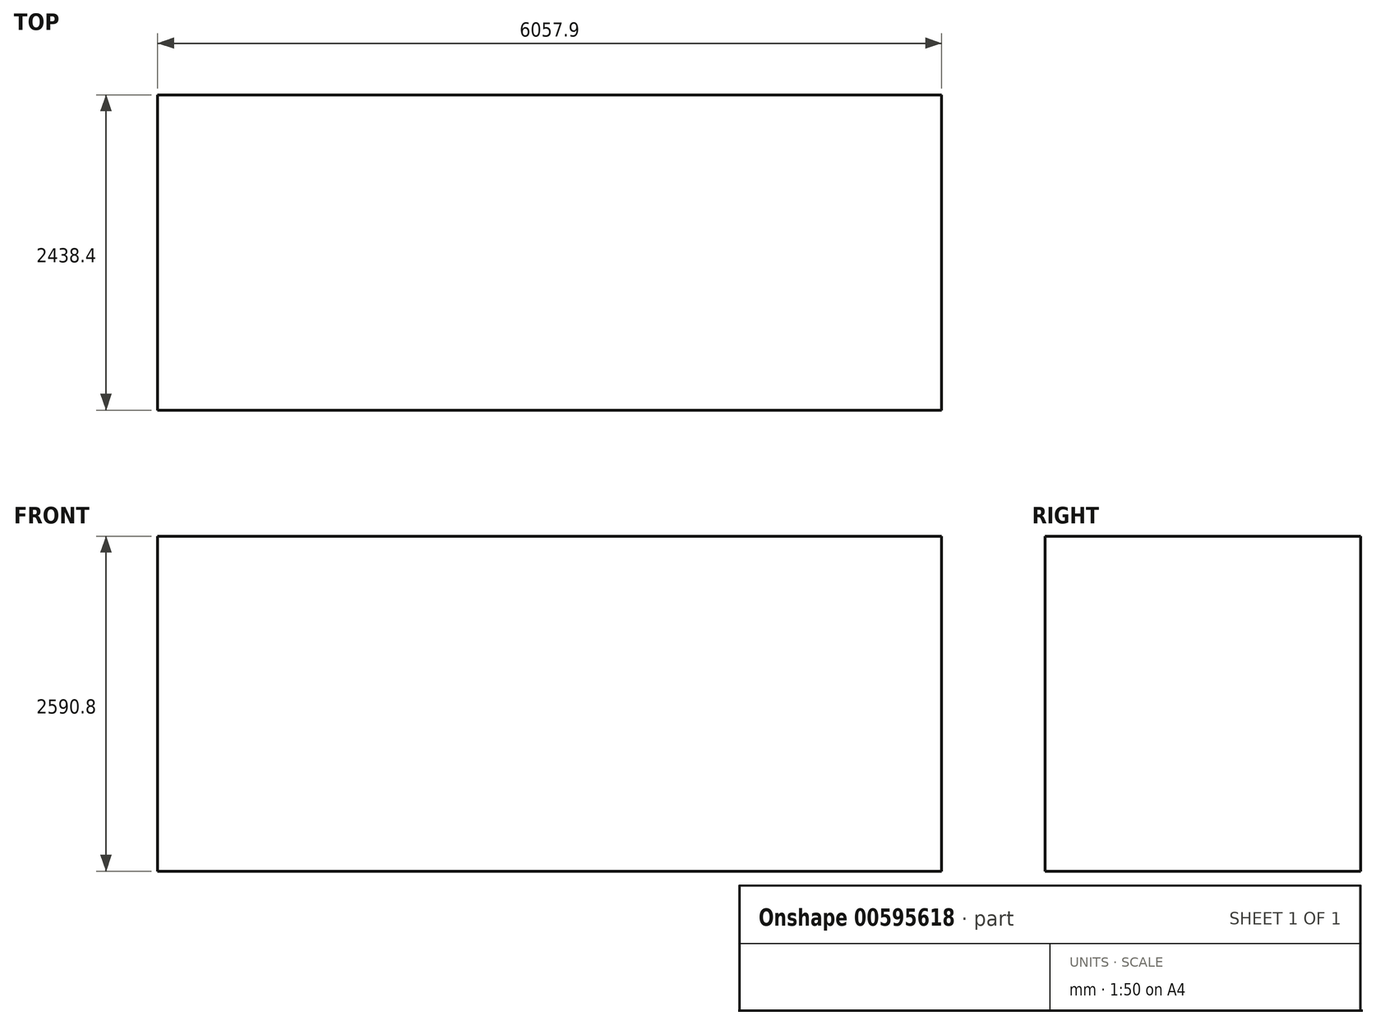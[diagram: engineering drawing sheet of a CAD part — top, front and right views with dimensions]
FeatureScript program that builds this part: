
annotation { "Feature Type Name" : "Feature", "Feature Type Description" : "" }
export const myFeature = defineFeature(function(context is Context, id is Id, definition is map)
    precondition{}
    {
        {
            var Q0;
            Q0=qCreatedBy(makeId("Top.planeOp"),FACE);
            var sketch = newSketch(context, id + "F0", { "sketchPlane" : qUnion([Q0])});
            skLineSegment(sketch, "E0.bottom", {"start": v(0, 0) * mm, "end": v(12192, 0) * mm});
            skLineSegment(sketch, "E0.top", {"start": v(0, 2438.4) * mm, "end": v(12192, 2438.4) * mm});
            skLineSegment(sketch, "E0.left", {"start": v(0, 0) * mm, "end": v(0, 2438.4) * mm});
            skLineSegment(sketch, "E0.right", {"start": v(12192, 0) * mm, "end": v(12192, 2438.4) * mm});
            skSolve(sketch);
        }
        {
            var Q0;
            Q0=makeQuery(id+"F0.imprint","IMPRINT",FACE,{"disambiguationData":[TD([[makeQuery(id+"F0.imprint","IMPRINT",EDGE,{"derivedFrom":sQuery(id+"F0.wireOp",EDGE,"E0.bottom")}),1.0]])]});
            extrude(context, id + "F1", {"entities" : qUnion([Q0]), "depth" : 2590.8 * mm, "offsetDistance" : 30.48 * mm});
        }
        {
            var Q0;
            Q0=makeQuery(id+"F1.opExtrude","SWEPT_BODY",BODY,{"disambiguationData":[OSD([sQuery(id+"F0.wireOp",EDGE,"E0.bottom"),sQuery(id+"F0.wireOp",EDGE,"E0.top"),sQuery(id+"F0.wireOp",EDGE,"E0.left"),sQuery(id+"F0.wireOp",EDGE,"E0.right")])]});
            transform(context, id + "F2", {"entities" : qUnion([Q0]), "transformType" : TransformType.COPY});
        }
        {
            var Q0;
            Q0=makeQuery(id+"F2.opPattern","COPY",FACE,{"derivedFrom":makeQuery(id+"F1.opExtrude","SWEPT_FACE",FACE,{"disambiguationData":[OSD([sQuery(id+"F0.wireOp",EDGE,"E0.right")])]}),"instanceName":"1"});
            extrude(context, id + "F3", {"entities" : qUnion([Q0]), "operationType" : NewBodyOperationType.REMOVE, "oppositeDirection" : true, "depth" : 6096 * mm + 38.1 * mm, "offsetDistance" : 30.48 * mm});
        }
    });
